# Revit family: OIZ
name_source: partatom
category: Mechanical Equipment
units: mm (PartAtom-declared; Revit-internal decimal feet)

## family parameters
Always vertical = Yes
Cut with Voids When Loaded = No
OmniClass Number = 23.40.40.11.17
OmniClass Title = Refrigerated Cases
Part Type = Normal
Room Calculation Point = No
Round Connector Dimension = Use Radius
Shared = No
Work Plane-Based = Yes

## types (3) — shared parameters
ANTI SWEAT APPARENT LOAD = 0 VA
ANTI SWEAT HEATER AMPS = 0 A
ANTI SWEAT HEATER WATTAGE = 0 W
BASE HEIGHT = 5"
BTU PER FOOT CONVENTIONAL = 509
BTU PER FOOT PARALLEL = 488
CERTIFICATIONS = NSF 7, UL471, CSA
COIL REFRIGERATION CHARGE = 0.00 lb
CONTROL TYPE = T-STAT
DATE = 04/18/2017
DEDICATED CIRCUIT = YES
DEFROST AMPS = 0 A
DEFROST PHASE = 1
DEFROST TIME AND DURATION = 2 @ 60 MIN
DEFROST WATTAGE = 0 W
DESIGNERS NAME = SHIDDRAMESH
DIEBOARD HEIGHT = 0"
DISCHARGE AIR TEMPERATURE = -4 °F
DRAIN LINE CONNECTION = Drain Connection
DRAIN LINE DIAMETER = 2"
DRAIN LINE RADIUS = 1"
DRAIN PIPE LENGTH = 0"
DRAIN PIPE TYPE = PVC
DRIP PAN PLUMB TYPE = HARD
Default Elevation = 48"
Description = Single-Deck Island Merchandiser
ELECTRIC DEFROST = No
ELECTRICAL DEFROST VOLTAGE = 0 V
EQUIPMENT MARK = OIZ
EVAPORATOR TEMPERATURE = -22 °F
FAN AMPS = 0 A
FAN AND ANTI SWEAT HEATER APPARENT LOAD = 0 VA
FAN APPARENT LOAD = 0 VA
FAN CONNECTOR DESCRIPTION = FAN AND ANTI SWEAT CONNECTOR
FAN NUMBER OF POLES = 1
FAN TYPE = ECM
FAN WATTAGE = 0 W
GROUND FAULT PROTECTION = NO
HEIGHT = 35 1/2"
HOT GAS DEFROST = No
ISOLATED GROUND REQUIRED = NO
Keynote = OIZ
LED LIGHTING AMPS = 0 A
LED LIGHTING AMPS PER ROW = 0 A
LED LIGHTING WATTAGE = 0 W
LEGEND NUMBER = OIZ-12'
LIGHT AMPS = 0 A
LIGHT TYPE = T8 FLUORESCENT
LIGHTING APPARENT LOAD = 0 VA
LIGHTING CONNECTION DESCRIPTION = LIGHTING CONNECTOR
LIGHTING NUMBER OF POLES = 1
LIGHTING WATTAGE = 0 VA
LIQUID LINE CONNECTION = LIQUID LINE CONNECTION
LIQUID LINE DIAMETER = 0"
LIQUID LINE RADIUS = 0"
Manufacturer = HILL PHOENIX
Model = OIZ-12'
NUMBER OF WIRES = 3
PHASE = 1
POWER FACTOR = 1
PRESSURE REGULATOR = 0.00 psi
RECEPTICAL MOUNTING HEIGHT ABOVE FLOOR = 0"
REF PLANE FRONT BACK = 28 7/16"
REVERSE AIR DEFROST = No
SANITARY PIPE SIZE = 1"
SET BACK MODE FOR ENERGY CONSERVATION = NO
SHELVE LENGTH = 48"
SIZE OF COLD WATER HOOK UP = 0"
SIZE OF HOT WATER HOOK-UP = 0"
SUCTION LINE CONNECTION = SUCTION LINE CONNECTION
SUCTION LINE DIAMETER = 1"
SUCTION LINE RADIUS = 0"
T8 LIGHT OR LED LIGHT = Yes
T8 LIGHTING AMPS = 0 A
T8 LIGHTING AMPS PER ROW = 0 A
T8 LIGHTING WATTAGE = 0 W
TIME OFF DEFROST = Yes
TOEKICK HEIGHT = 5 1/2"
TOEKICK INSET = 1 1/2"
TOTAL APPARENT FAN-LIGHT AND A/S LOAD = 0 VA
TOTAL CASE AMPS = 0 A
TOTAL CASE WATTAGE = 0 W
URL = http://www.hillphoenix.com
VOLTAGE = 0 V
WATER LINE MOUNTING HEIGHT ABOVE FLOOR = 0"
WEIGHT = 0.00 lb
WIDTH = 56 7/8"
zero-valued in all types: BTU ADD FOR LIGHTS, BTU ADD PER SHELF PER FOOT, CORNICE AND NOSE LIGHT ROWS, FAN QUANTITY, LED LIGHTING BTU ADD PER ROW, SHELF LIGHT ROWS, T8 LIGHTING BTU ADD PER ROW

## per-type parameters (varying)
| type | 12' END RETURN AIR GRILL | 8' END RETURN AIR GRILL | CONVENTIONAL EVAPORATOR LOAD | LENGTH | LENGTH FOR BTU | PARALLEL EVAPORATOR LOAD | REF PLANE LEFT RIGHT |
| OIZ-8' | No | Yes | 4072 | 96" | 8 | 3904 | 48" |
| OIZ-12' | Yes | No | 6108 | 144" | 12 | 5856 | 72" |
| OIZ - 4' | No | Yes | 2036 | 48" | 4 | 1952 | 24" |

## geometry (parser evidence)
native form markers: Blend x5, Sweep x2
no freeform markers — native parametric forms only
